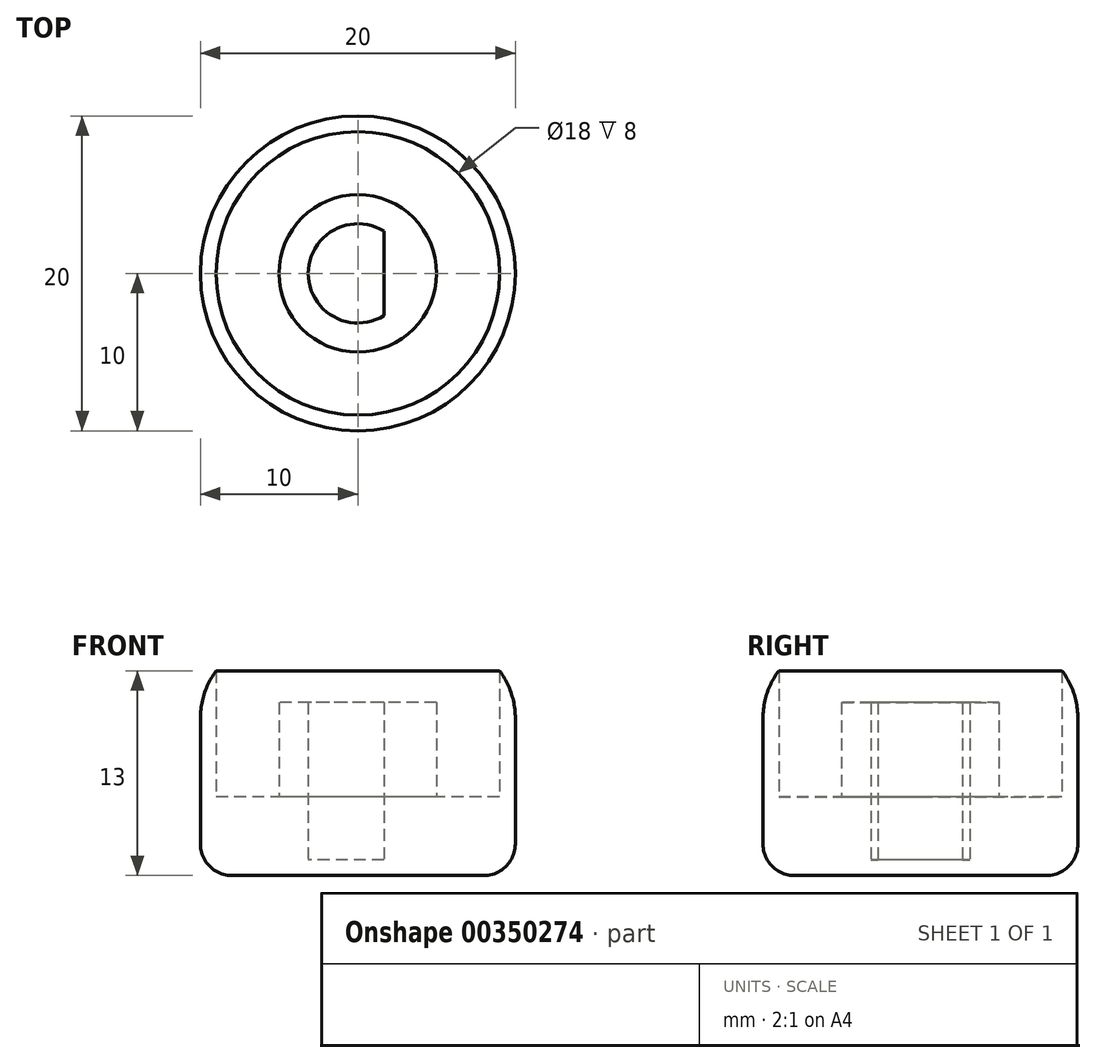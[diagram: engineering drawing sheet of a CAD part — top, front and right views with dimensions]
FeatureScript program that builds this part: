
annotation { "Feature Type Name" : "Feature", "Feature Type Description" : "" }
export const myFeature = defineFeature(function(context is Context, id is Id, definition is map)
    precondition{}
    {
        {
            var Q0;
            Q0=qCreatedBy(makeId("Top.planeOp"),FACE);
            var sketch = newSketch(context, id + "F0", { "sketchPlane" : qUnion([Q0])});
            skArc(sketch, "E0", {"start": v(1.65, 2.68) * mm, "mid": v(-3.15, 0) * mm, "end": v(1.65, -2.68) * mm});
            skLineSegment(sketch, "E1", {"start": v(1.65, 2.68) * mm, "end": v(1.65, -2.68) * mm});
            skCircle(sketch, "E2", {"center": v(0, 0) * mm, "radius": 10 * mm});
            skCircle(sketch, "E3", {"center": v(0, 0) * mm, "radius": 5 * mm});
            skSolve(sketch);
        }
        {
            var Q0;
            Q0 = qSketchRegion(id + "F0", true);
            extrude(context, id + "F1", {"entities" : qUnion([Q0]), "offsetDistance" : 25 * mm, "depth" : 4 * mm});
        }
        {
            var Q0;
            Q0=qCreatedBy(makeId("Top.planeOp"),FACE);
            var sketch = newSketch(context, id + "F2", { "sketchPlane" : qUnion([Q0])});
            skCircle(sketch, "E4", {"center": v(0, 0) * mm, "radius": 10 * mm});
            skCircle(sketch, "E5", {"center": v(0, 0) * mm, "radius": 9 * mm});
            skSolve(sketch);
        }
        {
            var Q0;
            Q0 = qSketchRegion(id + "F2", true);
            extrude(context, id + "F3", {"entities" : qUnion([Q0]), "operationType" : NewBodyOperationType.ADD, "depth" : 12 * mm});
        }
        {
            var Q0;
            Q0=makeQuery(id+"F3.opExtrude","CAP_EDGE",EDGE,{"disambiguationData":[OSD([sQuery(id+"F2.wireOp",EDGE,"E4")])],"isStart":false});
            fillet(context, id + "F4", {"entities" : qUnion([Q0]), "radius" : 5 * mm, "tangentPropagation" : true, "allowEdgeOverflow" : false});
        }
        {
            var Q0;
            Q0=makeQuery(id+"F0.imprint","IMPRINT",FACE,{"disambiguationData":[TD([[makeQuery(id+"F0.imprint","IMPRINT",EDGE,{"derivedFrom":sQuery(id+"F0.wireOp",EDGE,"E0")}),-1.0]])]});
            var sketch = newSketch(context, id + "F5", { "sketchPlane" : qUnion([Q0])});
            skCircle(sketch, "E6", {"center": v(0, 0) * mm, "radius": 10 * mm});
            skSolve(sketch);
        }
        {
            var Q0;
            Q0 = qSketchRegion(id + "F5", true);
            extrude(context, id + "F6", {"entities" : qUnion([Q0]), "operationType" : NewBodyOperationType.ADD, "oppositeDirection" : true, "depth" : 1 * mm});
        }
        {
            var Q0;
            Q0=makeQuery(id+"F6.opExtrude","CAP_FACE",FACE,{"disambiguationData":[OSD([sQuery(id+"F5.wireOp",EDGE,"E6")])],"isStart":false});
            fillet(context, id + "F7", {"entities" : qUnion([Q0]), "radius" : 2 * mm, "tangentPropagation" : true, "allowEdgeOverflow" : false});
        }
        {
            var Q0;
            Q0=makeQuery(id+"F0.imprint","IMPRINT",FACE,{"disambiguationData":[TD([[makeQuery(id+"F0.imprint","IMPRINT",EDGE,{"derivedFrom":sQuery(id+"F0.wireOp",EDGE,"E0")}),-1.0]])]});
            extrude(context, id + "F8", {"entities" : qUnion([Q0]), "operationType" : NewBodyOperationType.ADD, "depth" : 10 * mm, "offsetDistance" : 25 * mm});
        }
    });
